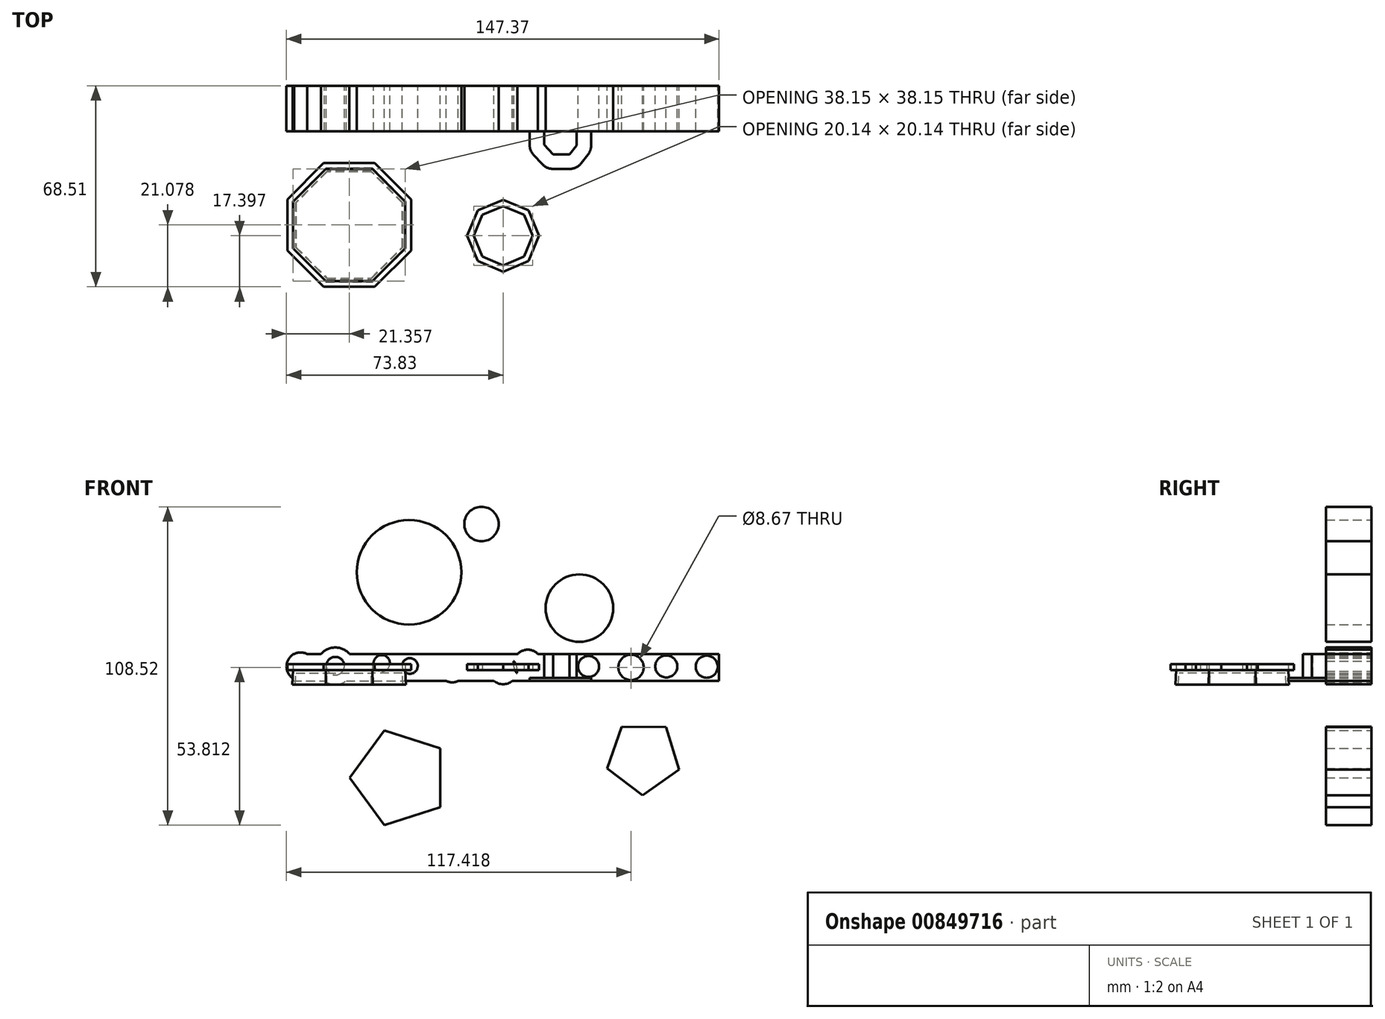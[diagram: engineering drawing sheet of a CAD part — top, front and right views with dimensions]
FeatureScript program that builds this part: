
annotation { "Feature Type Name" : "Feature", "Feature Type Description" : "" }
export const myFeature = defineFeature(function(context is Context, id is Id, definition is map)
    precondition{}
    {
        {
            var Q0;
            Q0=qCreatedBy(makeId("Front.planeOp"),FACE);
            var sketch = newSketch(context, id + "F0", { "sketchPlane" : qUnion([Q0])});
            skCircle(sketch, "E0", {"center": v(-32.06, 33.35) * mm, "radius": 17.81 * mm});
            skPoint(sketch, "E1.first.point", {"position": v(-14.26, 32.8) * mm});
            skCircle(sketch, "E2", {"center": v(26, 21.13) * mm, "radius": 11.5 * mm});
            skPoint(sketch, "E2.first.point", {"position": v(15.58, 26.02) * mm});
            skPoint(sketch, "E2.second.point", {"position": v(35.52, 14.67) * mm});
            skPoint(sketch, "E2.third.point", {"position": v(32.82, 30.4) * mm});
            skCircle(sketch, "E3.cCircle", {"center": v(-35.26, -36.7) * mm, "radius": 13.76 * mm, "construction": true});
            skLineSegment(sketch, "E3.0", {"start": v(-21.5, -26.7) * mm, "end": v(-21.5, -46.7) * mm});
            skLineSegment(sketch, "E3.1", {"start": v(-21.5, -46.7) * mm, "end": v(-40.52, -52.87) * mm});
            skLineSegment(sketch, "E3.2", {"start": v(-40.52, -52.87) * mm, "end": v(-52.27, -36.7) * mm});
            skLineSegment(sketch, "E3.3", {"start": v(-52.27, -36.7) * mm, "end": v(-40.52, -20.51) * mm});
            skLineSegment(sketch, "E3.4", {"start": v(-40.52, -20.51) * mm, "end": v(-21.5, -26.7) * mm});
            skLineSegment(sketch, "E4.0", {"start": v(-21.5, -40.98) * mm, "end": v(-21.5, -32.4) * mm});
            skPoint(sketch, "E4.0.midPoint", {"position": v(-21.5, -36.7) * mm});
            skCircle(sketch, "E5", {"center": v(-7.38, 49.79) * mm, "radius": 5.86 * mm});
            skCircle(sketch, "E6.cCircle", {"center": v(47.77, -29.76) * mm, "radius": 10.4 * mm, "construction": true});
            skLineSegment(sketch, "E6.0", {"start": v(59.94, -33.92) * mm, "end": v(47.58, -42.62) * mm});
            skLineSegment(sketch, "E6.1", {"start": v(47.58, -42.62) * mm, "end": v(35.48, -33.55) * mm});
            skLineSegment(sketch, "E6.2", {"start": v(35.48, -33.55) * mm, "end": v(40.37, -19.24) * mm});
            skLineSegment(sketch, "E6.3", {"start": v(40.37, -19.24) * mm, "end": v(55.49, -19.47) * mm});
            skLineSegment(sketch, "E6.4", {"start": v(55.49, -19.47) * mm, "end": v(59.94, -33.92) * mm});
            skPoint(sketch, "E6.0.midPoint", {"position": v(53.76, -38.27) * mm});
            skLineSegment(sketch, "E7.bottom", {"start": v(-71.72, 5.47) * mm, "end": v(73.54, 5.47) * mm});
            skLineSegment(sketch, "E7.top", {"start": v(-71.72, -3.64) * mm, "end": v(73.54, -3.64) * mm});
            skLineSegment(sketch, "E7.left", {"start": v(-71.72, 5.47) * mm, "end": v(-71.72, -3.64) * mm});
            skLineSegment(sketch, "E7.right", {"start": v(73.54, 5.47) * mm, "end": v(73.54, -3.64) * mm});
            skPoint(sketch, "E8", {"position": v(-69.03, 1.23) * mm});
            skPoint(sketch, "E9", {"position": v(-57.2, 1.43) * mm});
            skPoint(sketch, "E10", {"position": v(-41.37, 2.36) * mm});
            skPoint(sketch, "E11", {"position": v(-31.77, 1.42) * mm});
            skPoint(sketch, "E12", {"position": v(8.4, 2.1) * mm});
            skPoint(sketch, "E13", {"position": v(-17.33, 0) * mm});
            skPoint(sketch, "E14", {"position": v(29.1, 1.25) * mm});
            skPoint(sketch, "E15", {"position": v(55.6, 1.26) * mm});
            skPoint(sketch, "E16", {"position": v(69.39, 1.16) * mm});
            skPoint(sketch, "E17", {"position": v(43.59, 0.94) * mm});
            skCircle(sketch, "E18", {"center": v(69.39, 1.16) * mm, "radius": 3.76 * mm});
            skCircle(sketch, "E19", {"center": v(55.6, 1.26) * mm, "radius": 3.75 * mm});
            skCircle(sketch, "E20", {"center": v(43.59, 0.94) * mm, "radius": 4.33 * mm});
            skCircle(sketch, "E21", {"center": v(29.1, 1.25) * mm, "radius": 3.58 * mm});
            skCircle(sketch, "E22", {"center": v(8.4, 2.1) * mm, "radius": 4.85 * mm});
            skCircle(sketch, "E23", {"center": v(0, 0) * mm, "radius": 4.79 * mm});
            skCircle(sketch, "E24", {"center": v(-17.33, 0) * mm, "radius": 4.17 * mm});
            skCircle(sketch, "E25", {"center": v(-31.77, 1.42) * mm, "radius": 2.66 * mm});
            skCircle(sketch, "E26", {"center": v(-41.37, 2.36) * mm, "radius": 2.79 * mm});
            skCircle(sketch, "E27", {"center": v(-57.2, 1.43) * mm, "radius": 3.09 * mm});
            skCircle(sketch, "E28", {"center": v(-57.2, 1.43) * mm, "radius": 6.3 * mm});
            skCircle(sketch, "E29", {"center": v(-69.03, 1.23) * mm, "radius": 4.8 * mm});
            skSolve(sketch);
        }
        {
            var Q0;
            Q0 = qSketchRegion(id + "F0", true);
            extrude(context, id + "F1", {"entities" : qUnion([Q0]), "depth" : 15.5 * mm, "offsetDistance" : 25.4 * mm});
        }
        {
            var Q0;
            {var subQ0=sQuery(id+"F0.wireOp",EDGE,"E7.top");Q0=makeQuery(id+"F1.opExtrude","SWEPT_FACE",FACE,{"disambiguationData":[OSD([subQ0]),TDD([makeQuery(id+"F0.imprint","IMPRINT",EDGE,{"disambiguationData":[TD([[makeQuery(id+"F0.imprint","INTERSECT",VERTEX,{"derivedFrom":[subQ0,sQuery(id+"F0.wireOp",EDGE,"E7.right")]}),1.0]])],"derivedFrom":subQ0})])]});}
            var sketch = newSketch(context, id + "F2", { "sketchPlane" : qUnion([Q0])});
            skLineSegment(sketch, "E30", {"start": v(9.04, 15.5) * mm, "end": v(9.04, 20.1) * mm});
            skLineSegment(sketch, "E31", {"start": v(10.37, 23.5) * mm, "end": v(13.37, 26.73) * mm});
            skLineSegment(sketch, "E32", {"start": v(17.03, 28.33) * mm, "end": v(22.66, 28.33) * mm});
            skLineSegment(sketch, "E33", {"start": v(26.6, 26.4) * mm, "end": v(28.94, 23.42) * mm});
            skLineSegment(sketch, "E34", {"start": v(30, 20.34) * mm, "end": v(30, 15.5) * mm});
            skPoint(sketch, "E35.visualSharp", {"position": v(9.04, 22.06) * mm});
            skArc(sketch, "E35.filletArc", {"start": v(10.37, 23.5) * mm, "mid": v(9.38, 21.92) * mm, "end": v(9.04, 20.1) * mm});
            skPoint(sketch, "E36.visualSharp", {"position": v(14.85, 28.33) * mm});
            skArc(sketch, "E36.filletArc", {"start": v(17.03, 28.33) * mm, "mid": v(15.03, 27.91) * mm, "end": v(13.37, 26.73) * mm});
            skPoint(sketch, "E37.visualSharp", {"position": v(25.1, 28.33) * mm});
            skArc(sketch, "E37.filletArc", {"start": v(26.6, 26.4) * mm, "mid": v(24.85, 27.83) * mm, "end": v(22.66, 28.33) * mm});
            skPoint(sketch, "E38.visualSharp", {"position": v(30, 22.06) * mm});
            skArc(sketch, "E38.filletArc", {"start": v(30, 20.34) * mm, "mid": v(29.72, 21.97) * mm, "end": v(28.94, 23.42) * mm});
            skLineSegment(sketch, "E39.0", {"start": v(25, 20.34) * mm, "end": v(25, 15.5) * mm});
            skLineSegment(sketch, "E39.1", {"start": v(14.04, 15.5) * mm, "end": v(14.04, 20.1) * mm});
            skLineSegment(sketch, "E39.2", {"start": v(14.04, 20.1) * mm, "end": v(17.03, 23.33) * mm});
            skLineSegment(sketch, "E39.3", {"start": v(17.03, 23.33) * mm, "end": v(22.66, 23.33) * mm});
            skLineSegment(sketch, "E39.4", {"start": v(22.66, 23.33) * mm, "end": v(25, 20.34) * mm});
            skSolve(sketch);
        }
        {
            var Q0;
            {var subQ1=sQuery(id+"F2.wireOp",EDGE,"E39.0");Q0=makeQuery(id+"F2.imprint","IMPRINT",FACE,{"disambiguationData":[TD([[makeQuery(id+"F2.imprint","IMPRINT",EDGE,{"derivedFrom":subQ1}),-1.0]])]});}
            extrude(context, id + "F3", {"entities" : qUnion([Q0]), "operationType" : NewBodyOperationType.ADD, "oppositeDirection" : true, "depth" : 9.1 * mm, "offsetDistance" : 25 * mm});
        }
        {
            var Q0;
            {var subQ2=sQuery(id+"F2.wireOp",EDGE,"E30");Q0=makeQuery(id+"F2.imprint","IMPRINT",FACE,{"disambiguationData":[TD([[makeQuery(id+"F2.imprint","IMPRINT",EDGE,{"derivedFrom":subQ2}),-1.0]])]});}
            extrude(context, id + "F4", {"entities" : qUnion([Q0]), "operationType" : NewBodyOperationType.ADD, "oppositeDirection" : true, "depth" : 1 * mm, "offsetDistance" : 25 * mm});
        }
        {
            var Q0;
            Q0=qCreatedBy(makeId("Top.planeOp"),FACE);
            var sketch = newSketch(context, id + "F5", { "sketchPlane" : qUnion([Q0])});
            skLineSegment(sketch, "E40", {"start": v(15.48, -51.11) * mm, "end": v(-15.48, -51.11) * mm, "construction": true});
            skLineSegment(sketch, "E41", {"start": v(0, -51.11) * mm, "end": v(8.13, -42.98) * mm, "construction": true});
            skPoint(sketch, "E41.startSnap0", {"position": v(0, -51.11) * mm});
            skLineSegment(sketch, "E42", {"start": v(0, -51.11) * mm, "end": v(5.68, -37.4) * mm, "construction": true});
            skLineSegment(sketch, "E43", {"start": v(3.56, -42.52) * mm, "end": v(0, -41.04) * mm});
            skLineSegment(sketch, "E44.MirrorCS", {"start": v(3.56, -42.52) * mm, "end": v(7.12, -44) * mm, "construction": true});
            skLineSegment(sketch, "E45.MirrorCS", {"start": v(8.6, -47.55) * mm, "end": v(7.12, -44) * mm});
            skLineSegment(sketch, "E46.MirrorCS", {"start": v(8.6, -47.55) * mm, "end": v(10.07, -51.11) * mm});
            skLineSegment(sketch, "E47.MirrorCS", {"start": v(8.6, -54.67) * mm, "end": v(10.07, -51.11) * mm, "construction": true});
            skLineSegment(sketch, "E48.MirrorCS", {"start": v(8.6, -54.67) * mm, "end": v(7.12, -58.23) * mm, "construction": true});
            skLineSegment(sketch, "E49.MirrorCS", {"start": v(3.56, -59.7) * mm, "end": v(7.12, -58.23) * mm, "construction": true});
            skLineSegment(sketch, "E50.MirrorCS", {"start": v(3.56, -59.7) * mm, "end": v(0, -61.18) * mm, "construction": true});
            skLineSegment(sketch, "E51.MirrorCS", {"start": v(3.56, -42.52) * mm, "end": v(0, -41.04) * mm, "construction": true});
            skLineSegment(sketch, "E52.MirrorCS", {"start": v(8.6, -47.55) * mm, "end": v(7.12, -44) * mm, "construction": true});
            skLineSegment(sketch, "E53.MirrorCS", {"start": v(8.6, -47.55) * mm, "end": v(10.07, -51.11) * mm, "construction": true});
            skLineSegment(sketch, "E54.MirrorCS", {"start": v(0, -51.11) * mm, "end": v(8.13, -59.25) * mm, "construction": true});
            skLineSegment(sketch, "E55.MirrorCS", {"start": v(8.6, -54.67) * mm, "end": v(7.12, -58.23) * mm});
            skLineSegment(sketch, "E56.MirrorCS", {"start": v(3.56, -42.52) * mm, "end": v(7.12, -44) * mm});
            skLineSegment(sketch, "E57.MirrorCS", {"start": v(0, -51.11) * mm, "end": v(5.68, -64.83) * mm, "construction": true});
            skLineSegment(sketch, "E58.MirrorCS", {"start": v(3.56, -59.7) * mm, "end": v(7.12, -58.23) * mm});
            skLineSegment(sketch, "E59.MirrorCS", {"start": v(3.56, -59.7) * mm, "end": v(0, -61.18) * mm});
            skLineSegment(sketch, "E60.MirrorCS", {"start": v(8.6, -54.67) * mm, "end": v(10.07, -51.11) * mm});
            skLineSegment(sketch, "E61.MirrorCS", {"start": v(-3.56, -59.7) * mm, "end": v(0, -61.18) * mm});
            skLineSegment(sketch, "E62.MirrorCS", {"start": v(-3.56, -59.7) * mm, "end": v(-7.12, -58.23) * mm});
            skLineSegment(sketch, "E63.MirrorCS", {"start": v(-8.6, -54.67) * mm, "end": v(-7.12, -58.23) * mm});
            skLineSegment(sketch, "E64.MirrorCS", {"start": v(-8.6, -54.67) * mm, "end": v(-10.07, -51.11) * mm});
            skLineSegment(sketch, "E65.MirrorCS", {"start": v(-8.6, -47.55) * mm, "end": v(-10.07, -51.11) * mm});
            skLineSegment(sketch, "E66.MirrorCS", {"start": v(-8.6, -47.55) * mm, "end": v(-7.12, -44) * mm});
            skLineSegment(sketch, "E67.MirrorCS", {"start": v(-3.56, -42.52) * mm, "end": v(0, -41.04) * mm});
            skLineSegment(sketch, "E68.MirrorCS", {"start": v(-3.56, -42.52) * mm, "end": v(-7.12, -44) * mm});
            skLineSegment(sketch, "E69.0", {"start": v(10.44, -46.79) * mm, "end": v(12.23, -51.11) * mm});
            skLineSegment(sketch, "E69.1", {"start": v(10.44, -55.44) * mm, "end": v(12.23, -51.11) * mm});
            skLineSegment(sketch, "E69.2", {"start": v(10.44, -55.44) * mm, "end": v(8.65, -59.76) * mm});
            skLineSegment(sketch, "E69.3", {"start": v(4.33, -61.56) * mm, "end": v(8.65, -59.76) * mm});
            skLineSegment(sketch, "E69.4", {"start": v(4.33, -61.56) * mm, "end": v(0, -63.35) * mm});
            skLineSegment(sketch, "E69.5", {"start": v(-4.33, -40.67) * mm, "end": v(-8.65, -42.46) * mm});
            skLineSegment(sketch, "E69.6", {"start": v(-4.33, -40.67) * mm, "end": v(0, -38.88) * mm});
            skLineSegment(sketch, "E69.7", {"start": v(4.33, -40.67) * mm, "end": v(0, -38.88) * mm});
            skLineSegment(sketch, "E69.8", {"start": v(4.33, -40.67) * mm, "end": v(8.65, -42.46) * mm});
            skLineSegment(sketch, "E69.9", {"start": v(-10.44, -46.79) * mm, "end": v(-8.65, -42.46) * mm});
            skLineSegment(sketch, "E69.10", {"start": v(-10.44, -46.79) * mm, "end": v(-12.23, -51.11) * mm});
            skLineSegment(sketch, "E69.11", {"start": v(-10.44, -55.44) * mm, "end": v(-12.23, -51.11) * mm});
            skLineSegment(sketch, "E69.12", {"start": v(-10.44, -55.44) * mm, "end": v(-8.65, -59.76) * mm});
            skLineSegment(sketch, "E69.13", {"start": v(-4.33, -61.56) * mm, "end": v(-8.65, -59.76) * mm});
            skLineSegment(sketch, "E69.14", {"start": v(10.44, -46.79) * mm, "end": v(8.65, -42.46) * mm});
            skLineSegment(sketch, "E69.15", {"start": v(-4.33, -61.56) * mm, "end": v(0, -63.35) * mm});
            skCircle(sketch, "E70.cCircle", {"center": v(-52.47, -47.43) * mm, "radius": 21.08 * mm, "construction": true});
            skLineSegment(sketch, "E70.0", {"start": v(-31.4, -56.16) * mm, "end": v(-43.74, -68.5) * mm});
            skLineSegment(sketch, "E70.1", {"start": v(-43.74, -68.5) * mm, "end": v(-61.2, -68.5) * mm});
            skLineSegment(sketch, "E70.2", {"start": v(-61.2, -68.5) * mm, "end": v(-73.55, -56.16) * mm});
            skLineSegment(sketch, "E70.3", {"start": v(-73.55, -56.16) * mm, "end": v(-73.55, -38.7) * mm});
            skLineSegment(sketch, "E70.4", {"start": v(-73.55, -38.7) * mm, "end": v(-61.2, -26.36) * mm});
            skLineSegment(sketch, "E70.5", {"start": v(-61.2, -26.36) * mm, "end": v(-43.74, -26.36) * mm});
            skLineSegment(sketch, "E70.6", {"start": v(-43.74, -26.36) * mm, "end": v(-31.4, -38.7) * mm});
            skLineSegment(sketch, "E70.7", {"start": v(-31.4, -38.7) * mm, "end": v(-31.4, -56.16) * mm});
            skPoint(sketch, "E70.0.midPoint", {"position": v(-37.57, -62.34) * mm});
            skLineSegment(sketch, "E71.0", {"start": v(-71.55, -55.33) * mm, "end": v(-71.55, -39.53) * mm});
            skLineSegment(sketch, "E71.1", {"start": v(-60.37, -66.5) * mm, "end": v(-71.55, -55.33) * mm});
            skLineSegment(sketch, "E71.2", {"start": v(-71.55, -39.53) * mm, "end": v(-60.37, -28.36) * mm});
            skLineSegment(sketch, "E71.3", {"start": v(-44.57, -66.5) * mm, "end": v(-60.37, -66.5) * mm});
            skLineSegment(sketch, "E71.4", {"start": v(-60.37, -28.36) * mm, "end": v(-44.57, -28.36) * mm});
            skLineSegment(sketch, "E71.5", {"start": v(-44.57, -28.36) * mm, "end": v(-33.4, -39.53) * mm});
            skLineSegment(sketch, "E71.6", {"start": v(-33.4, -39.53) * mm, "end": v(-33.4, -55.33) * mm});
            skLineSegment(sketch, "E71.7", {"start": v(-33.4, -55.33) * mm, "end": v(-44.57, -66.5) * mm});
            skSolve(sketch);
        }
        {
            var Q0;
            Q0 = qSketchRegion(id + "F5", true);
            extrude(context, id + "F6", {"entities" : qUnion([Q0]), "depth" : 2 * mm, "offsetDistance" : 25 * mm});
        }
        {
            var Q0;
            Q0=makeQuery(id+"F6.opExtrude","CAP_FACE",FACE,{"disambiguationData":[OSD([sQuery(id+"F5.wireOp",EDGE,"E70.0"),sQuery(id+"F5.wireOp",EDGE,"E70.1"),sQuery(id+"F5.wireOp",EDGE,"E70.2"),sQuery(id+"F5.wireOp",EDGE,"E70.3"),sQuery(id+"F5.wireOp",EDGE,"E70.4"),sQuery(id+"F5.wireOp",EDGE,"E70.5"),sQuery(id+"F5.wireOp",EDGE,"E70.6"),sQuery(id+"F5.wireOp",EDGE,"E70.7"),sQuery(id+"F5.wireOp",EDGE,"E71.0"),sQuery(id+"F5.wireOp",EDGE,"E71.1"),sQuery(id+"F5.wireOp",EDGE,"E71.2"),sQuery(id+"F5.wireOp",EDGE,"E71.3"),sQuery(id+"F5.wireOp",EDGE,"E71.4"),sQuery(id+"F5.wireOp",EDGE,"E71.5"),sQuery(id+"F5.wireOp",EDGE,"E71.6"),sQuery(id+"F5.wireOp",EDGE,"E71.7")])],"isStart":true});
            var sketch = newSketch(context, id + "F7", { "sketchPlane" : qUnion([Q0])});
            skSolve(sketch);
        }
        {
            var Q0;
            Q0=makeQuery(id+"F7.imprint","IMPRINT",FACE,{"disambiguationData":[TD([[makeQuery(id+"F7.imprint","IMPRINT",EDGE,{"derivedFrom":makeQuery(id+"F6.opExtrude","CAP_EDGE",EDGE,{"disambiguationData":[OSD([sQuery(id+"F5.wireOp",EDGE,"E71.0")])],"isStart":true})}),1.0]])]});
            extrude(context, id + "F8", {"entities" : qUnion([Q0]), "depth" : 5 * mm, "offsetDistance" : 25 * mm, "hasDraft" : true, "draftAngle" : 3 * degree});
        }
        {
            var Q0;
            Q0=makeQuery(id+"F8.opExtrude","CAP_FACE",FACE,{"disambiguationData":[OSD([sQuery(id+"F5.wireOp",EDGE,"E71.0"),sQuery(id+"F5.wireOp",EDGE,"E71.1"),sQuery(id+"F5.wireOp",EDGE,"E71.2"),sQuery(id+"F5.wireOp",EDGE,"E71.3"),sQuery(id+"F5.wireOp",EDGE,"E71.4"),sQuery(id+"F5.wireOp",EDGE,"E71.5"),sQuery(id+"F5.wireOp",EDGE,"E71.6"),sQuery(id+"F5.wireOp",EDGE,"E71.7")])],"isStart":false});
            shell(context, id + "F9", {"entities" : qUnion([Q0]), "thickness" : 1 * mm});
        }
    });
